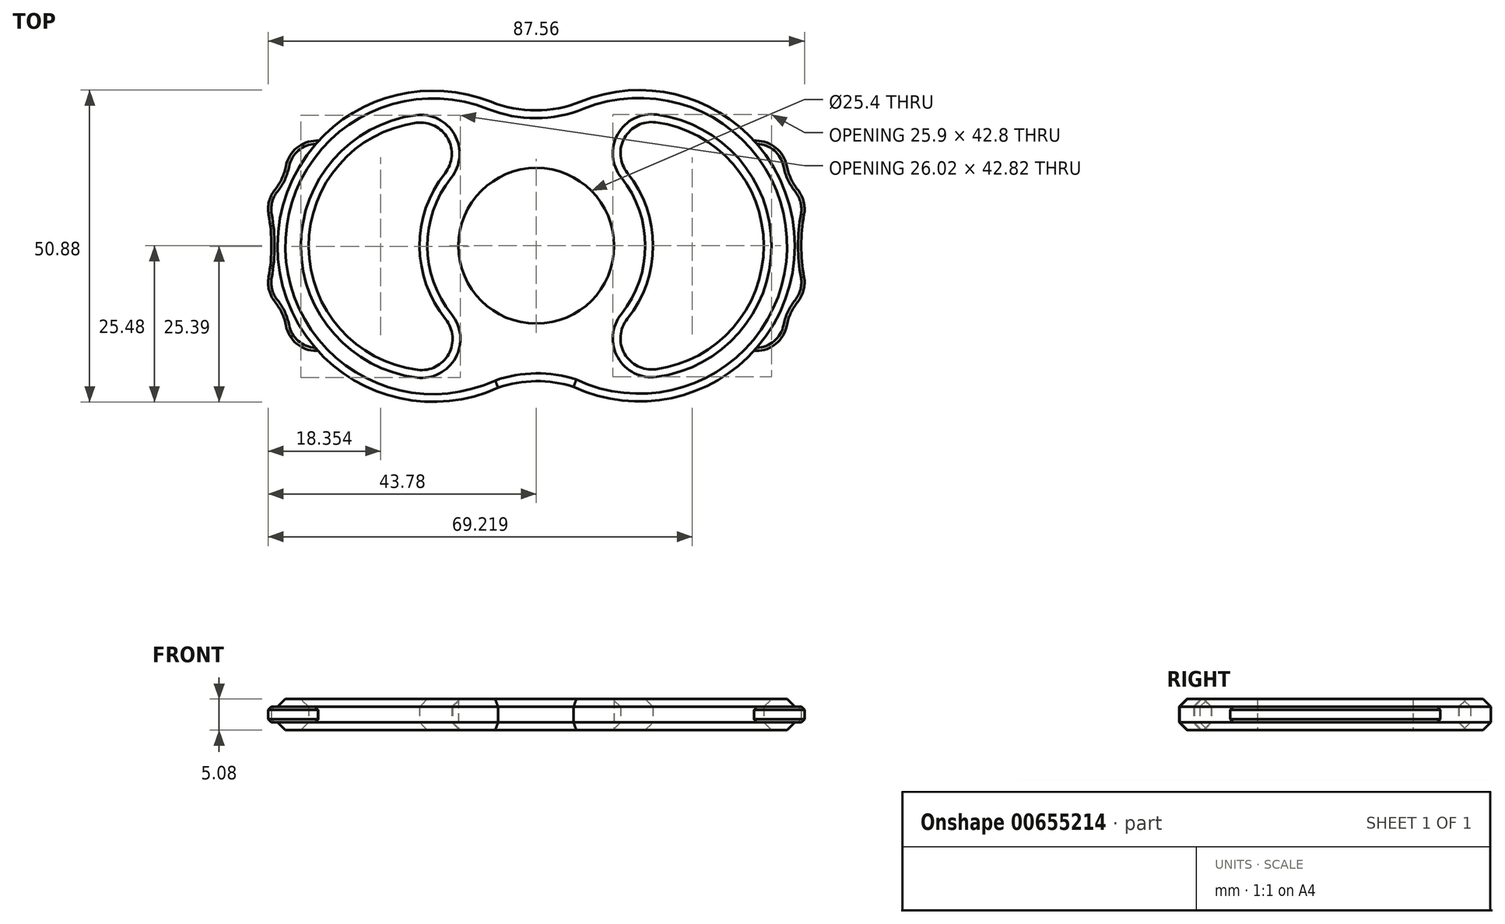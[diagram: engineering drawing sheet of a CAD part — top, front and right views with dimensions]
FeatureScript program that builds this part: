
annotation { "Feature Type Name" : "Feature", "Feature Type Description" : "" }
export const myFeature = defineFeature(function(context is Context, id is Id, definition is map)
    precondition{}
    {
        {
            var Q0;
            Q0=qCreatedBy(makeId("Top.planeOp"),FACE);
            var sketch = newSketch(context, id + "F0", { "sketchPlane" : qUnion([Q0])});
            skCircle(sketch, "E0", {"center": v(0, 0) * mm, "radius": 12.7 * mm});
            skCircle(sketch, "E1", {"center": v(0, 0) * mm, "radius": 19.05 * mm});
            skArc(sketch, "E2", {"start": v(0, -19.05) * mm, "mid": v(42.2, 0) * mm, "end": v(0, 19.05) * mm});
            skArc(sketch, "E3.0", {"start": v(2.5, -14.44) * mm, "mid": v(37.12, 0) * mm, "end": v(2.5, 14.44) * mm});
            skArc(sketch, "E4.1.0", {"start": v(-2.55, 14.36) * mm, "mid": v(-37.17, -0.08) * mm, "end": v(-2.55, -14.52) * mm});
            skArc(sketch, "E4.1.1", {"start": v(-0.05, 18.97) * mm, "mid": v(-42.25, -0.08) * mm, "end": v(-0.05, -19.13) * mm});
            skPoint(sketch, "E4.center", {"position": v(-0.02, -0.04) * mm});
            skArc(sketch, "E5", {"start": v(-7.4, 23.5) * mm, "mid": v(-0.07, 22.1) * mm, "end": v(7.24, 23.53) * mm});
            skArc(sketch, "E6.1.0", {"start": v(7.4, -23.5) * mm, "mid": v(0.07, -22.1) * mm, "end": v(-7.24, -23.53) * mm});
            skSolve(sketch);
        }
        {
            var Q0;
            Q0 = qSketchRegion(id + "F0", true);
            var Q1;
            Q1=makeQuery(id+"F0.imprint","IMPRINT",FACE,{"disambiguationData":[TD([[makeQuery(id+"F0.imprint","IMPRINT",EDGE,{"derivedFrom":sQuery(id+"F0.wireOp",EDGE,"E0")}),-1.0]])]});
            extrude(context, id + "F1", {"entities" : qUnion([Q0, Q1]), "depth" : 5.08 * mm, "offsetDistance" : 25.4 * mm});
        }
        {
            var Q0;
            {var subQ0=sQuery(id+"F0.wireOp",EDGE,"E3.0");var subQ1=sQuery(id+"F0.wireOp",EDGE,"E1");Q0=makeQuery(id+"F1.opExtrude","SWEPT_EDGE",EDGE,{"disambiguationData":[OSD([subQ1,subQ0]),TDD([makeQuery(id+"F0.imprint","INTERSECT",VERTEX,{"disambiguationData":[OD(0.0)],"derivedFrom":[subQ1,subQ0]})])]});}
            var Q1;
            {var subQ0=sQuery(id+"F0.wireOp",EDGE,"E3.0");var subQ1=sQuery(id+"F0.wireOp",EDGE,"E1");Q1=makeQuery(id+"F1.opExtrude","SWEPT_EDGE",EDGE,{"disambiguationData":[OSD([subQ1,subQ0]),TDD([makeQuery(id+"F0.imprint","INTERSECT",VERTEX,{"disambiguationData":[OD(1.0)],"derivedFrom":[subQ1,subQ0]})])]});}
            var Q2;
            {var subQ0=sQuery(id+"F0.wireOp",EDGE,"E4.1.0");var subQ1=sQuery(id+"F0.wireOp",EDGE,"E1");Q2=makeQuery(id+"F1.opExtrude","SWEPT_EDGE",EDGE,{"disambiguationData":[OSD([subQ1,subQ0]),TDD([makeQuery(id+"F0.imprint","INTERSECT",VERTEX,{"disambiguationData":[OD(0.0)],"derivedFrom":[subQ1,subQ0]})])]});}
            var Q3;
            {var subQ0=sQuery(id+"F0.wireOp",EDGE,"E4.1.0");var subQ1=sQuery(id+"F0.wireOp",EDGE,"E1");Q3=makeQuery(id+"F1.opExtrude","SWEPT_EDGE",EDGE,{"disambiguationData":[OSD([subQ1,subQ0]),TDD([makeQuery(id+"F0.imprint","INTERSECT",VERTEX,{"disambiguationData":[OD(1.0)],"derivedFrom":[subQ1,subQ0]})])]});}
            fillet(context, id + "F2", {"entities" : qUnion([Q0, Q1, Q2, Q3]), "radius" : 5.08 * mm, "tangentPropagation" : true, "allowEdgeOverflow" : false});
        }
        {
            var Q0;
            Q0=makeQuery(id+"F1.opExtrude","CAP_EDGE",EDGE,{"disambiguationData":[OSD([sQuery(id+"F0.wireOp",EDGE,"E4.1.1")])],"isStart":false});
            var Q1;
            Q1=makeQuery(id+"F1.opExtrude","CAP_EDGE",EDGE,{"disambiguationData":[OSD([sQuery(id+"F0.wireOp",EDGE,"E6.1.0")])],"isStart":false});
            var Q2;
            Q2=makeQuery(id+"F1.opExtrude","CAP_EDGE",EDGE,{"disambiguationData":[OSD([sQuery(id+"F0.wireOp",EDGE,"E4.1.0")])],"isStart":false});
            var Q3;
            {var subQ0=sQuery(id+"F0.wireOp",EDGE,"E3.0");var subQ1=sQuery(id+"F0.wireOp",EDGE,"E1");Q3=makeQuery(id+"F1.opExtrude","CAP_EDGE",EDGE,{"disambiguationData":[OSD([subQ1]),TDD([makeQuery(id+"F0.imprint","IMPRINT",EDGE,{"disambiguationData":[TD([[makeQuery(id+"F0.imprint","INTERSECT",VERTEX,{"disambiguationData":[OD(0.0)],"derivedFrom":[subQ1,subQ0]}),1.0]])],"derivedFrom":subQ1})])],"isStart":false});}
            var Q4;
            Q4=makeQuery(id+"F1.opExtrude","CAP_EDGE",EDGE,{"disambiguationData":[OSD([sQuery(id+"F0.wireOp",EDGE,"E2")])],"isStart":true});
            var Q5;
            Q5=makeQuery(id+"F1.opExtrude","CAP_EDGE",EDGE,{"disambiguationData":[OSD([sQuery(id+"F0.wireOp",EDGE,"E6.1.0")])],"isStart":true});
            var Q6;
            {var subQ0=sQuery(id+"F0.wireOp",EDGE,"E3.0");var subQ1=sQuery(id+"F0.wireOp",EDGE,"E1");Q6=makeQuery(id+"F1.opExtrude","CAP_EDGE",EDGE,{"disambiguationData":[OSD([subQ1]),TDD([makeQuery(id+"F0.imprint","IMPRINT",EDGE,{"disambiguationData":[TD([[makeQuery(id+"F0.imprint","INTERSECT",VERTEX,{"disambiguationData":[OD(0.0)],"derivedFrom":[subQ1,subQ0]}),1.0]])],"derivedFrom":subQ1})])],"isStart":true});}
            var Q7;
            {var subQ0=sQuery(id+"F0.wireOp",EDGE,"E4.1.0");var subQ1=sQuery(id+"F0.wireOp",EDGE,"E1");Q7=makeQuery(id+"F1.opExtrude","CAP_EDGE",EDGE,{"disambiguationData":[OSD([subQ1]),TDD([makeQuery(id+"F0.imprint","IMPRINT",EDGE,{"disambiguationData":[TD([[makeQuery(id+"F0.imprint","INTERSECT",VERTEX,{"disambiguationData":[OD(0.0)],"derivedFrom":[subQ1,subQ0]}),-1.0]])],"derivedFrom":subQ1})])],"isStart":true});}
            chamfer(context, id + "F3", {"entities" : qUnion([Q0, Q1, Q2, Q3, Q4, Q5, Q6, Q7]), "width" : 1.27 * mm, "tangentPropagation" : true});
        }
        {
            var Q0;
            Q0=qCreatedBy(makeId("Top.planeOp"),FACE);
            cPlane(context, id + "F4", {"entities" : qUnion([Q0]), "cplaneType" : CPlaneType.OFFSET, "offset" : 1.27 * mm, "width" : 152.4 * mm, "height" : 152.4 * mm});
        }
        {
            var Q0;
            Q0=qCreatedBy(id+"F4.planeOp",FACE);
            var sketch = newSketch(context, id + "F5", { "sketchPlane" : qUnion([Q0])});
            skLineSegment(sketch, "E7", {"start": v(39.02, 0) * mm, "end": v(39.02, 11.53) * mm});
            skLineSegment(sketch, "E8", {"start": v(39.02, 0) * mm, "end": v(39.02, -11.53) * mm});
            skLineSegment(sketch, "E9", {"start": v(39.02, -11.53) * mm, "end": v(44.27, -7.61) * mm});
            skLineSegment(sketch, "E10", {"start": v(44.27, 7.61) * mm, "end": v(39.02, 11.53) * mm});
            skLineSegment(sketch, "E11", {"start": v(44.27, -7.61) * mm, "end": v(42.18, 0) * mm});
            skLineSegment(sketch, "E12", {"start": v(42.18, 0) * mm, "end": v(44.27, 7.61) * mm});
            skLineSegment(sketch, "E13", {"start": v(39.02, 0) * mm, "end": v(42.18, 0) * mm});
            skLineSegment(sketch, "E14", {"start": v(39.02, -11.53) * mm, "end": v(34.31, -17.15) * mm});
            skLineSegment(sketch, "E15", {"start": v(34.31, -17.15) * mm, "end": v(41.03, -17.15) * mm});
            skLineSegment(sketch, "E16", {"start": v(41.03, -17.15) * mm, "end": v(39.02, -11.53) * mm});
            skLineSegment(sketch, "E17", {"start": v(39.02, 11.53) * mm, "end": v(34.31, 17.15) * mm});
            skLineSegment(sketch, "E18", {"start": v(34.31, 17.15) * mm, "end": v(41.03, 17.15) * mm});
            skLineSegment(sketch, "E19", {"start": v(41.03, 17.15) * mm, "end": v(39.02, 11.53) * mm});
            skArc(sketch, "E20", {"start": v(41.03, 17.15) * mm, "mid": v(41.17, 11.88) * mm, "end": v(44.27, 7.61) * mm});
            skArc(sketch, "E21.MirrorCS", {"start": v(41.03, -17.15) * mm, "mid": v(41.17, -11.88) * mm, "end": v(44.27, -7.61) * mm});
            skArc(sketch, "E22", {"start": v(44.27, 7.61) * mm, "mid": v(43.24, 0) * mm, "end": v(44.27, -7.61) * mm});
            skArc(sketch, "E23.1.0", {"start": v(-41.03, 17.15) * mm, "mid": v(-41.17, 11.88) * mm, "end": v(-44.27, 7.61) * mm});
            skLineSegment(sketch, "E23.1.1", {"start": v(-39.02, 11.53) * mm, "end": v(-34.31, 17.15) * mm});
            skLineSegment(sketch, "E23.1.2", {"start": v(-34.31, 17.15) * mm, "end": v(-41.03, 17.15) * mm});
            skLineSegment(sketch, "E23.1.3", {"start": v(-39.02, 0) * mm, "end": v(-39.02, 11.53) * mm});
            skArc(sketch, "E23.1.4", {"start": v(-44.27, -7.61) * mm, "mid": v(-43.24, 0) * mm, "end": v(-44.27, 7.61) * mm});
            skLineSegment(sketch, "E23.1.5", {"start": v(-39.02, 0) * mm, "end": v(-39.02, -11.53) * mm});
            skArc(sketch, "E23.1.6", {"start": v(-41.03, -17.15) * mm, "mid": v(-41.17, -11.88) * mm, "end": v(-44.27, -7.61) * mm});
            skLineSegment(sketch, "E23.1.7", {"start": v(-39.02, -11.53) * mm, "end": v(-34.31, -17.15) * mm});
            skLineSegment(sketch, "E23.1.8", {"start": v(-34.31, -17.15) * mm, "end": v(-41.03, -17.15) * mm});
            skPoint(sketch, "E23.center", {"position": v(0, 0) * mm});
            skSolve(sketch);
        }
        {
            var Q0;
            Q0 = qSketchRegion(id + "F5", true);
            extrude(context, id + "F6", {"entities" : qUnion([Q0]), "operationType" : NewBodyOperationType.ADD, "depth" : 2.54 * mm, "offsetDistance" : 25.4 * mm});
        }
        {
            var Q0;
            Q0=makeQuery(id+"F6.opExtrude","SWEPT_EDGE",EDGE,{"disambiguationData":[OSD([sQuery(id+"F5.wireOp",EDGE,"E10"),sQuery(id+"F5.wireOp",EDGE,"E12"),sQuery(id+"F5.wireOp",EDGE,"E20"),sQuery(id+"F5.wireOp",EDGE,"E22")])]});
            var Q1;
            Q1=makeQuery(id+"F6.opExtrude","SWEPT_EDGE",EDGE,{"disambiguationData":[OSD([sQuery(id+"F5.wireOp",EDGE,"E18"),sQuery(id+"F5.wireOp",EDGE,"E19"),sQuery(id+"F5.wireOp",EDGE,"E20")])]});
            var Q2;
            Q2=makeQuery(id+"F6.opExtrude","SWEPT_EDGE",EDGE,{"disambiguationData":[OSD([sQuery(id+"F5.wireOp",EDGE,"E9"),sQuery(id+"F5.wireOp",EDGE,"E11"),sQuery(id+"F5.wireOp",EDGE,"E21.MirrorCS"),sQuery(id+"F5.wireOp",EDGE,"E22")])]});
            var Q3;
            Q3=makeQuery(id+"F6.opExtrude","SWEPT_EDGE",EDGE,{"disambiguationData":[OSD([sQuery(id+"F5.wireOp",EDGE,"E15"),sQuery(id+"F5.wireOp",EDGE,"E16"),sQuery(id+"F5.wireOp",EDGE,"E21.MirrorCS")])]});
            var Q4;
            Q4=makeQuery(id+"F6.opExtrude","SWEPT_EDGE",EDGE,{"disambiguationData":[OSD([sQuery(id+"F5.wireOp",EDGE,"E23.1.0"),sQuery(id+"F5.wireOp",EDGE,"E23.1.2")])]});
            var Q5;
            Q5=makeQuery(id+"F6.opExtrude","SWEPT_EDGE",EDGE,{"disambiguationData":[OSD([sQuery(id+"F5.wireOp",EDGE,"E23.1.0"),sQuery(id+"F5.wireOp",EDGE,"E23.1.4")])]});
            var Q6;
            Q6=makeQuery(id+"F6.opExtrude","SWEPT_EDGE",EDGE,{"disambiguationData":[OSD([sQuery(id+"F5.wireOp",EDGE,"E23.1.4"),sQuery(id+"F5.wireOp",EDGE,"E23.1.6")])]});
            var Q7;
            Q7=makeQuery(id+"F6.opExtrude","SWEPT_EDGE",EDGE,{"disambiguationData":[OSD([sQuery(id+"F5.wireOp",EDGE,"E23.1.6"),sQuery(id+"F5.wireOp",EDGE,"E23.1.8")])]});
            fillet(context, id + "F7", {"entities" : qUnion([Q0, Q1, Q2, Q3, Q4, Q5, Q6, Q7]), "radius" : 5.08 * mm, "tangentPropagation" : true, "allowEdgeOverflow" : false});
        }
        {
            var Q0;
            Q0=makeQuery(id+"F6.opExtrude","CAP_EDGE",EDGE,{"disambiguationData":[OSD([sQuery(id+"F5.wireOp",EDGE,"E22")])],"isStart":true});
            var Q1;
            Q1=makeQuery(id+"F6.opExtrude","CAP_EDGE",EDGE,{"disambiguationData":[OSD([sQuery(id+"F5.wireOp",EDGE,"E22")])],"isStart":false});
            var Q2;
            Q2=makeQuery(id+"F6.opExtrude","CAP_EDGE",EDGE,{"disambiguationData":[OSD([sQuery(id+"F5.wireOp",EDGE,"E23.1.4")])],"isStart":true});
            var Q3;
            Q3=makeQuery(id+"F6.opExtrude","CAP_EDGE",EDGE,{"disambiguationData":[OSD([sQuery(id+"F5.wireOp",EDGE,"E23.1.4")])],"isStart":false});
            chamfer(context, id + "F8", {"entities" : qUnion([Q0, Q1, Q2, Q3]), "width" : 0.5 * mm, "tangentPropagation" : true});
        }
    });
